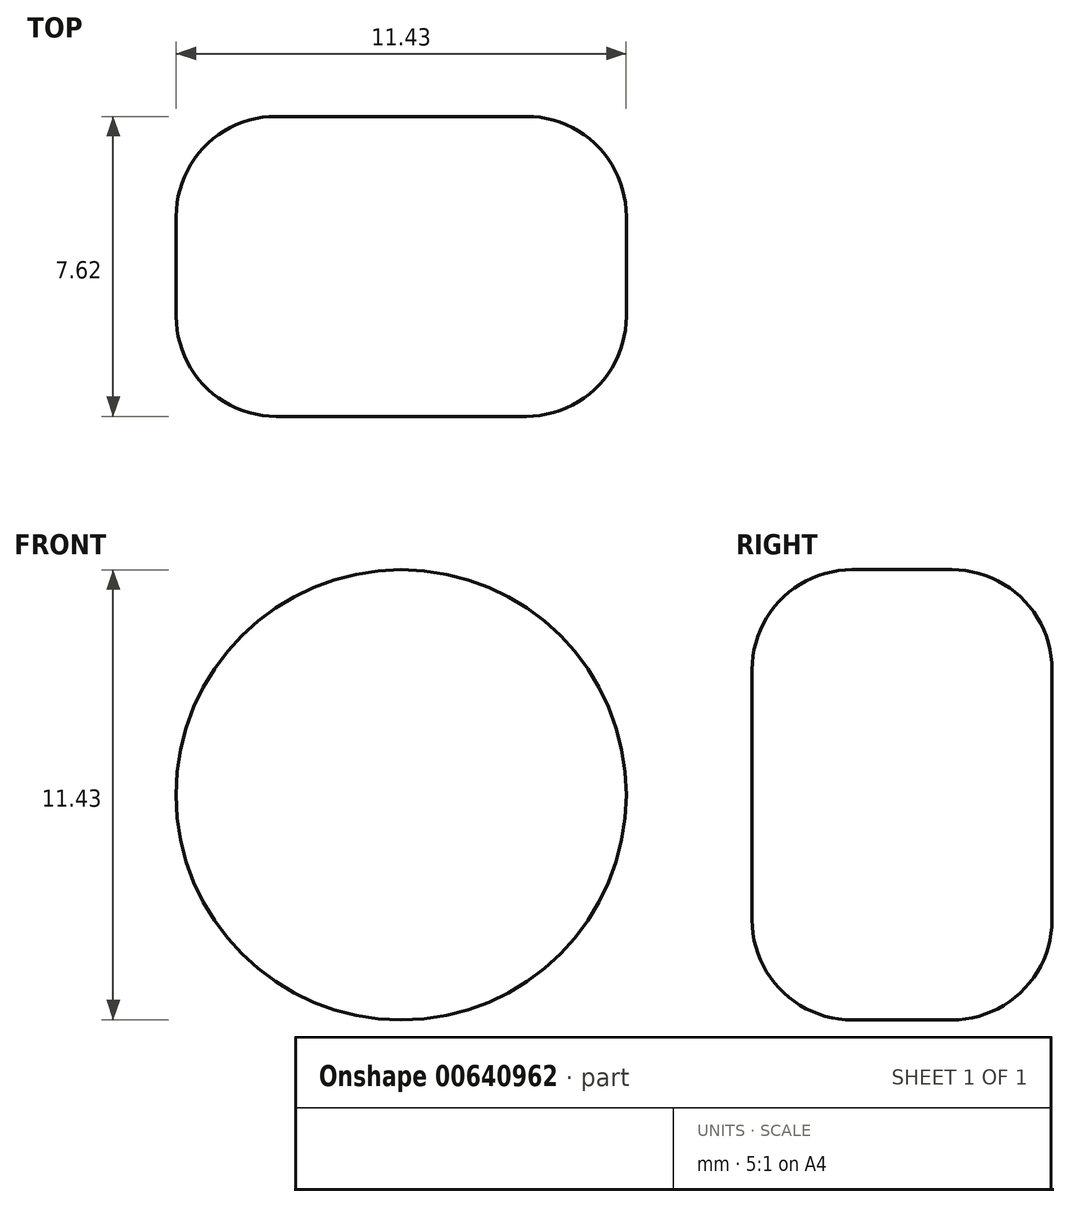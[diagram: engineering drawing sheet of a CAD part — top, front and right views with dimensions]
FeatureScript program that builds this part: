
annotation { "Feature Type Name" : "Feature", "Feature Type Description" : "" }
export const myFeature = defineFeature(function(context is Context, id is Id, definition is map)
    precondition{}
    {
        {
            var Q0;
            Q0=qCreatedBy(makeId("Front.planeOp"),FACE);
            var sketch = newSketch(context, id + "F0", { "sketchPlane" : qUnion([Q0])});
            skCircle(sketch, "E0", {"center": v(-53.44, 27.4) * mm, "radius": 5.72 * mm});
            skSolve(sketch);
        }
        {
            var Q0;
            Q0=makeQuery(id+"F0.imprint","IMPRINT",FACE,{"disambiguationData":[TD([[makeQuery(id+"F0.imprint","IMPRINT",EDGE,{"derivedFrom":sQuery(id+"F0.wireOp",EDGE,"E0")}),1.0]])]});
            extrude(context, id + "F1", {"entities" : qUnion([Q0]), "depth" : 7.62 * mm, "offsetDistance" : 25.4 * mm});
        }
        {
            var Q0;
            Q0=makeQuery(id+"F1.opExtrude","CAP_FACE",FACE,{"disambiguationData":[OSD([sQuery(id+"F0.wireOp",EDGE,"E0")])],"isStart":false});
            fillet(context, id + "F2", {"entities" : qUnion([Q0]), "radius" : 2.54 * mm, "tangentPropagation" : true, "allowEdgeOverflow" : false});
        }
        {
            var Q0;
            Q0=makeQuery(id+"F1.opExtrude","CAP_FACE",FACE,{"disambiguationData":[OSD([sQuery(id+"F0.wireOp",EDGE,"E0")])],"isStart":true});
            fillet(context, id + "F3", {"entities" : qUnion([Q0]), "radius" : 2.54 * mm, "tangentPropagation" : true, "allowEdgeOverflow" : false});
        }
    });
